FCSTD DOCUMENT  (FreeCAD 0.17R13541 (Git))
Label: qd_device_parts_v2
License: All rights reserved
LicenseURL: http://en.wikipedia.org/wiki/All_rights_reserved
objects: Sketcher::SketchObject×30, Part::Feature×24, App::DocumentObjectGroup×1
note: 54 computed .brp shape members not serialized (recipe doc carries the construction recipe); baked Part::Feature solids carry a one-line shape summary decoded from their .brp

FEATURE [App::DocumentObjectGroup] qqd_v2_6  label="qqd-v2-6"
FEATURE [Part::Feature] Shape
  shape: bbox 3400 x 150 x 2e-07 mm, 0 faces, 0 solids (baked)
FEATURE [Part::Feature] Shape001
  shape: bbox 1400 x 856.2 x 2e-07 mm, 0 faces, 0 solids (baked)
FEATURE [Part::Feature] Shape002
  shape: bbox 842.8 x 945 x 2e-07 mm, 0 faces, 0 solids (baked)
FEATURE [Part::Feature] Shape003
  shape: bbox 1400 x 856.2 x 2e-07 mm, 0 faces, 0 solids (baked)
FEATURE [Part::Feature] Shape004
  shape: bbox 1400 x 856.2 x 2e-07 mm, 0 faces, 0 solids (baked)
FEATURE [Part::Feature] Shape005
  shape: bbox 1400 x 856.2 x 2e-07 mm, 0 faces, 0 solids (baked)
FEATURE [Part::Feature] Shape006
  shape: bbox 2530 x 825 x 2e-07 mm, 0 faces, 0 solids (baked)
FEATURE [Part::Feature] Shape007
  shape: bbox 1180 x 825 x 2e-07 mm, 0 faces, 0 solids (baked)
FEATURE [Part::Feature] Shape008
  shape: bbox 1180 x 825 x 2e-07 mm, 0 faces, 0 solids (baked)
FEATURE [Part::Feature] Shape009
  shape: bbox 225 x 945 x 2e-07 mm, 0 faces, 0 solids (baked)
FEATURE [Part::Feature] Shape010
  shape: bbox 495 x 945 x 2e-07 mm, 0 faces, 0 solids (baked)
FEATURE [Part::Feature] Shape011
  shape: bbox 360 x 945 x 2e-07 mm, 0 faces, 0 solids (baked)
FEATURE [Part::Feature] Shape012
  shape: bbox 630 x 945 x 2e-07 mm, 0 faces, 0 solids (baked)
FEATURE [Part::Feature] Shape013
  shape: bbox 150 x 945 x 2e-07 mm, 0 faces, 0 solids (baked)
FEATURE [Part::Feature] Shape014
  shape: bbox 360 x 945 x 2e-07 mm, 0 faces, 0 solids (baked)
FEATURE [Part::Feature] Shape015
  shape: bbox 630 x 945 x 2e-07 mm, 0 faces, 0 solids (baked)
FEATURE [Part::Feature] Shape016
  shape: bbox 225 x 945 x 2e-07 mm, 0 faces, 0 solids (baked)
FEATURE [Part::Feature] Shape017
  shape: bbox 495 x 945 x 2e-07 mm, 0 faces, 0 solids (baked)
FEATURE [Part::Feature] Shape018
  shape: bbox 584 x 945 x 2e-07 mm, 0 faces, 0 solids (baked)
FEATURE [Part::Feature] Shape019
  shape: bbox 780 x 945 x 2e-07 mm, 0 faces, 0 solids (baked)
FEATURE [Part::Feature] Shape020
  shape: bbox 679 x 945 x 2e-07 mm, 0 faces, 0 solids (baked)
FEATURE [Part::Feature] Shape021
  shape: bbox 679 x 945 x 2e-07 mm, 0 faces, 0 solids (baked)
FEATURE [Part::Feature] Shape022
  shape: bbox 780 x 945 x 2e-07 mm, 0 faces, 0 solids (baked)
FEATURE [Part::Feature] Shape023
  shape: bbox 584 x 945 x 2e-07 mm, 0 faces, 0 solids (baked)
FEATURE [Sketcher::SketchObject] Sketch
  sketch-geometry (4):
    g0: LineSegment StartX=1699.91 StartY=105 StartZ=0 EndX=-1699.91 EndY=105 EndZ=0
    g1: LineSegment StartX=-1699.91 StartY=105 StartZ=0 EndX=-1699.91 EndY=-45 EndZ=0
    g2: LineSegment StartX=-1699.91 StartY=-45 StartZ=0 EndX=1699.91 EndY=-45 EndZ=0
    g3: LineSegment StartX=1699.91 StartY=-45 StartZ=0 EndX=1699.91 EndY=105 EndZ=0
  constraints (8):
    c: Horizontal(g0)
    c: Coincident(g0,g1)
    c: Vertical(g1)
    c: Coincident(g1,g2)
    c: Horizontal(g2)
    c: Coincident(g2,g3)
    c: Vertical(g3)
    c: Coincident(g3,g0)
FEATURE [Sketcher::SketchObject] Sketch001
  sketch-geometry (7):
    g0: LineSegment StartX=450 StartY=-970 StartZ=0 EndX=170 EndY=-185 EndZ=0
    g1: LineSegment StartX=170 StartY=-185 StartZ=0 EndX=170 EndY=-25 EndZ=0
    g2: LineSegment StartX=170 StartY=-25 StartZ=0 EndX=90 EndY=-25 EndZ=0
    g3: LineSegment StartX=90 StartY=-25 StartZ=0 EndX=90 EndY=-145 EndZ=0
    g4: LineSegment StartX=90 StartY=-145 StartZ=0 EndX=133.61 EndY=-355.94 EndZ=0
    g5: LineSegment StartX=133.61 StartY=-355.94 StartZ=0 EndX=300 EndY=-970 EndZ=0
    g6: LineSegment StartX=300 StartY=-970 StartZ=0 EndX=450 EndY=-970 EndZ=0
  constraints (11):
    c: Coincident(g0,g1)
    c: Vertical(g1)
    c: Coincident(g1,g2)
    c: Horizontal(g2)
    c: Coincident(g2,g3)
    c: Vertical(g3)
    c: Coincident(g3,g4)
    c: Coincident(g4,g5)
    c: Coincident(g5,g6)
    c: Horizontal(g6)
    c: Coincident(g6,g0)
FEATURE [Sketcher::SketchObject] Sketch002
  sketch-geometry (6):
    g0: LineSegment StartX=-40 StartY=-205 StartZ=0 EndX=-40 EndY=-25 EndZ=0
    g1: LineSegment StartX=-40 StartY=-25 StartZ=0 EndX=40 EndY=-25 EndZ=0
    g2: LineSegment StartX=40 StartY=-25 StartZ=0 EndX=40 EndY=-205 EndZ=0
    g3: LineSegment StartX=40 StartY=-205 StartZ=0 EndX=75 EndY=-970 EndZ=0
    g4: LineSegment StartX=75 StartY=-970 StartZ=0 EndX=-75 EndY=-970 EndZ=0
    g5: LineSegment StartX=-75 StartY=-970 StartZ=0 EndX=-40 EndY=-205 EndZ=0
  constraints (10):
    c: Vertical(g0)
    c: Coincident(g0,g1)
    c: Horizontal(g1)
    c: Coincident(g1,g2)
    c: Vertical(g2)
    c: Coincident(g2,g3)
    c: Coincident(g3,g4)
    c: Horizontal(g4)
    c: Coincident(g4,g5)
    c: Coincident(g5,g0)
FEATURE [Sketcher::SketchObject] Sketch003
  sketch-geometry (8):
    g0: LineSegment StartX=-369.81 StartY=-145 StartZ=0 EndX=369.81 EndY=-145 EndZ=0
    g1: LineSegment StartX=369.81 StartY=-145 StartZ=0 EndX=1265 EndY=-970 EndZ=0
    g2: LineSegment StartX=1265 StartY=-970 StartZ=0 EndX=905 EndY=-970 EndZ=0
    g3: LineSegment StartX=905 StartY=-970 StartZ=0 EndX=448.323 EndY=-535 EndZ=0
    g4: LineSegment StartX=448.323 StartY=-535 StartZ=0 EndX=-448.323 EndY=-535 EndZ=0
    g5: LineSegment StartX=-448.323 StartY=-535 StartZ=0 EndX=-905 EndY=-970 EndZ=0
    g6: LineSegment StartX=-905 StartY=-970 StartZ=0 EndX=-1265 EndY=-970 EndZ=0
    g7: LineSegment StartX=-1265 StartY=-970 StartZ=0 EndX=-369.81 EndY=-145 EndZ=0
  constraints (12):
    c: Horizontal(g0)
    c: Coincident(g0,g1)
    c: Coincident(g1,g2)
    c: Horizontal(g2)
    c: Coincident(g2,g3)
    c: Coincident(g3,g4)
    c: Horizontal(g4)
    c: Coincident(g4,g5)
    c: Coincident(g5,g6)
    c: Horizontal(g6)
    c: Coincident(g6,g7)
    c: Coincident(g7,g0)
FEATURE [Sketcher::SketchObject] Sketch004
  sketch-geometry (7):
    g0: LineSegment StartX=-450 StartY=-970 StartZ=0 EndX=-170 EndY=-185 EndZ=0
    g1: LineSegment StartX=-170 StartY=-185 StartZ=0 EndX=-170 EndY=-25 EndZ=0
    g2: LineSegment StartX=-170 StartY=-25 StartZ=0 EndX=-90 EndY=-25 EndZ=0
    g3: LineSegment StartX=-90 StartY=-25 StartZ=0 EndX=-90 EndY=-145 EndZ=0
    g4: LineSegment StartX=-90 StartY=-145 StartZ=0 EndX=-133.61 EndY=-355.94 EndZ=0
    g5: LineSegment StartX=-133.61 StartY=-355.94 StartZ=0 EndX=-300 EndY=-970 EndZ=0
    g6: LineSegment StartX=-300 StartY=-970 StartZ=0 EndX=-450 EndY=-970 EndZ=0
  constraints (11):
    c: Coincident(g0,g1)
    c: Vertical(g1)
    c: Coincident(g1,g2)
    c: Horizontal(g2)
    c: Coincident(g2,g3)
    c: Vertical(g3)
    c: Coincident(g3,g4)
    c: Coincident(g4,g5)
    c: Coincident(g5,g6)
    c: Horizontal(g6)
    c: Coincident(g6,g0)
FEATURE [Sketcher::SketchObject] Sketch005
  sketch-geometry (7):
    g0: LineSegment StartX=-105 StartY=-25 StartZ=0 EndX=-25 EndY=-25 EndZ=0
    g1: LineSegment StartX=-25 StartY=-25 StartZ=0 EndX=-25 EndY=-145 EndZ=0
    g2: LineSegment StartX=-25 StartY=-145 StartZ=0 EndX=-53.655 EndY=-503.461 EndZ=0
    g3: LineSegment StartX=-53.655 StartY=-503.461 StartZ=0 EndX=-100 EndY=-970 EndZ=0
    g4: LineSegment StartX=-100 StartY=-970 StartZ=0 EndX=-250 EndY=-970 EndZ=0
    g5: LineSegment StartX=-250 StartY=-970 StartZ=0 EndX=-105 EndY=-205 EndZ=0
    g6: LineSegment StartX=-105 StartY=-205 StartZ=0 EndX=-105 EndY=-25 EndZ=0
  constraints (11):
    c: Horizontal(g0)
    c: Coincident(g0,g1)
    c: Vertical(g1)
    c: Coincident(g1,g2)
    c: Coincident(g2,g3)
    c: Coincident(g3,g4)
    c: Horizontal(g4)
    c: Coincident(g4,g5)
    c: Coincident(g5,g6)
    c: Vertical(g6)
    c: Coincident(g6,g0)
FEATURE [Sketcher::SketchObject] Sketch006
  sketch-geometry (7):
    g0: LineSegment StartX=-251.765 StartY=595 StartZ=0 EndX=-448.323 EndY=595 EndZ=0
    g1: LineSegment StartX=-448.323 StartY=595 StartZ=0 EndX=-905 EndY=1030 EndZ=0
    g2: LineSegment StartX=-905 StartY=1030 StartZ=0 EndX=-1265 EndY=1030 EndZ=0
    g3: LineSegment StartX=-1265 StartY=1030 StartZ=0 EndX=-369.81 EndY=205 EndZ=0
    g4: LineSegment StartX=-369.81 StartY=205 StartZ=0 EndX=-85 EndY=205 EndZ=0
    g5: LineSegment StartX=-85 StartY=205 StartZ=0 EndX=-85 EndY=265 EndZ=0
    g6: LineSegment StartX=-85 StartY=265 StartZ=0 EndX=-251.765 EndY=595 EndZ=0
  constraints (11):
    c: Horizontal(g0)
    c: Coincident(g0,g1)
    c: Coincident(g1,g2)
    c: Horizontal(g2)
    c: Coincident(g2,g3)
    c: Coincident(g3,g4)
    c: Horizontal(g4)
    c: Coincident(g4,g5)
    c: Vertical(g5)
    c: Coincident(g5,g6)
    c: Coincident(g6,g0)
FEATURE [Sketcher::SketchObject] Sketch007
  sketch-geometry (8):
    g0: LineSegment StartX=-1685.36 StartY=-431.669 StartZ=0 EndX=-1198.72 EndY=-881.17 EndZ=0
    g1: LineSegment StartX=-1198.72 StartY=-881.17 StartZ=0 EndX=-720.86 EndY=-499.639 EndZ=0
    g2: LineSegment StartX=-720.86 StartY=-499.639 StartZ=0 EndX=-362.004 EndY=-165 EndZ=0
    g3: LineSegment StartX=-362.004 StartY=-165 StartZ=0 EndX=-305 EndY=-165 EndZ=0
    g4: LineSegment StartX=-305 StartY=-165 StartZ=0 EndX=-285 EndY=-145 EndZ=0
    g5: LineSegment StartX=-285 StartY=-145 StartZ=0 EndX=-285 EndY=-25 EndZ=0
    g6: LineSegment StartX=-285 StartY=-25 StartZ=0 EndX=-859.697 EndY=-25 EndZ=0
    g7: LineSegment StartX=-859.697 StartY=-25 StartZ=0 EndX=-1685.36 EndY=-431.669 EndZ=0
  constraints (11):
    c: Coincident(g0,g1)
    c: Coincident(g1,g2)
    c: Coincident(g2,g3)
    c: Horizontal(g3)
    c: Coincident(g3,g4)
    c: Coincident(g4,g5)
    c: Vertical(g5)
    c: Coincident(g5,g6)
    c: Horizontal(g6)
    c: Coincident(g6,g7)
    c: Coincident(g7,g0)
FEATURE [Sketcher::SketchObject] Sketch008
  sketch-geometry (8):
    g0: LineSegment StartX=1685.36 StartY=-431.669 StartZ=0 EndX=1198.72 EndY=-881.17 EndZ=0
    g1: LineSegment StartX=1198.72 StartY=-881.17 StartZ=0 EndX=720.86 EndY=-499.639 EndZ=0
    g2: LineSegment StartX=720.86 StartY=-499.639 StartZ=0 EndX=362.004 EndY=-165 EndZ=0
    g3: LineSegment StartX=362.004 StartY=-165 StartZ=0 EndX=305 EndY=-165 EndZ=0
    g4: LineSegment StartX=305 StartY=-165 StartZ=0 EndX=285 EndY=-145 EndZ=0
    g5: LineSegment StartX=285 StartY=-145 StartZ=0 EndX=285 EndY=-25 EndZ=0
    g6: LineSegment StartX=285 StartY=-25 StartZ=0 EndX=859.697 EndY=-25 EndZ=0
    g7: LineSegment StartX=859.697 StartY=-25 StartZ=0 EndX=1685.36 EndY=-431.669 EndZ=0
  constraints (11):
    c: Coincident(g0,g1)
    c: Coincident(g1,g2)
    c: Coincident(g2,g3)
    c: Horizontal(g3)
    c: Coincident(g3,g4)
    c: Coincident(g4,g5)
    c: Vertical(g5)
    c: Coincident(g5,g6)
    c: Horizontal(g6)
    c: Coincident(g6,g7)
    c: Coincident(g7,g0)
FEATURE [Sketcher::SketchObject] Sketch009
  sketch-geometry (8):
    g0: LineSegment StartX=-1685.36 StartY=491.669 StartZ=0 EndX=-1198.72 EndY=941.17 EndZ=0
    g1: LineSegment StartX=-1198.72 StartY=941.17 StartZ=0 EndX=-720.86 EndY=559.639 EndZ=0
    g2: LineSegment StartX=-720.86 StartY=559.639 StartZ=0 EndX=-362.004 EndY=225 EndZ=0
    g3: LineSegment StartX=-362.004 StartY=225 StartZ=0 EndX=-305 EndY=225 EndZ=0
    g4: LineSegment StartX=-305 StartY=225 StartZ=0 EndX=-285 EndY=205 EndZ=0
    g5: LineSegment StartX=-285 StartY=205 StartZ=0 EndX=-285 EndY=85 EndZ=0
    g6: LineSegment StartX=-285 StartY=85 StartZ=0 EndX=-859.697 EndY=85 EndZ=0
    g7: LineSegment StartX=-859.697 StartY=85 StartZ=0 EndX=-1685.36 EndY=491.669 EndZ=0
  constraints (11):
    c: Coincident(g0,g1)
    c: Coincident(g1,g2)
    c: Coincident(g2,g3)
    c: Horizontal(g3)
    c: Coincident(g3,g4)
    c: Coincident(g4,g5)
    c: Vertical(g5)
    c: Coincident(g5,g6)
    c: Horizontal(g6)
    c: Coincident(g6,g7)
    c: Coincident(g7,g0)
FEATURE [Sketcher::SketchObject] Sketch010
  sketch-geometry (8):
    g0: LineSegment StartX=402.551 StartY=853.805 StartZ=0 EndX=105 EndY=265 EndZ=0
    g1: LineSegment StartX=105 StartY=265 StartZ=0 EndX=105 EndY=85 EndZ=0
    g2: LineSegment StartX=105 StartY=85 StartZ=0 EndX=-105 EndY=85 EndZ=0
    g3: LineSegment StartX=-105 StartY=85 StartZ=0 EndX=-105 EndY=265 EndZ=0
    g4: LineSegment StartX=-105 StartY=265 StartZ=0 EndX=-402.551 EndY=853.805 EndZ=0
    g5: LineSegment StartX=-402.551 StartY=853.805 StartZ=0 EndX=-421.41 EndY=1030 EndZ=0
    g6: LineSegment StartX=-421.41 StartY=1030 StartZ=0 EndX=421.41 EndY=1030 EndZ=0
    g7: LineSegment StartX=421.41 StartY=1030 StartZ=0 EndX=402.551 EndY=853.805 EndZ=0
  constraints (12):
    c: Coincident(g0,g1)
    c: Vertical(g1)
    c: Coincident(g1,g2)
    c: Horizontal(g2)
    c: Coincident(g2,g3)
    c: Vertical(g3)
    c: Coincident(g3,g4)
    c: Coincident(g4,g5)
    c: Coincident(g5,g6)
    c: Horizontal(g6)
    c: Coincident(g6,g7)
    c: Coincident(g7,g0)
FEATURE [Sketcher::SketchObject] Sketch011
  sketch-geometry (7):
    g0: LineSegment StartX=251.765 StartY=595 StartZ=0 EndX=448.323 EndY=595 EndZ=0
    g1: LineSegment StartX=448.323 StartY=595 StartZ=0 EndX=905 EndY=1030 EndZ=0
    g2: LineSegment StartX=905 StartY=1030 StartZ=0 EndX=1265 EndY=1030 EndZ=0
    g3: LineSegment StartX=1265 StartY=1030 StartZ=0 EndX=369.81 EndY=205 EndZ=0
    g4: LineSegment StartX=369.81 StartY=205 StartZ=0 EndX=85 EndY=205 EndZ=0
    g5: LineSegment StartX=85 StartY=205 StartZ=0 EndX=85 EndY=265 EndZ=0
    g6: LineSegment StartX=85 StartY=265 StartZ=0 EndX=251.765 EndY=595 EndZ=0
  constraints (11):
    c: Horizontal(g0)
    c: Coincident(g0,g1)
    c: Coincident(g1,g2)
    c: Horizontal(g2)
    c: Coincident(g2,g3)
    c: Coincident(g3,g4)
    c: Horizontal(g4)
    c: Coincident(g4,g5)
    c: Vertical(g5)
    c: Coincident(g5,g6)
    c: Coincident(g6,g0)
FEATURE [Sketcher::SketchObject] Sketch012
  sketch-geometry (8):
    g0: LineSegment StartX=1685.36 StartY=491.669 StartZ=0 EndX=1198.72 EndY=941.17 EndZ=0
    g1: LineSegment StartX=1198.72 StartY=941.17 StartZ=0 EndX=720.86 EndY=559.639 EndZ=0
    g2: LineSegment StartX=720.86 StartY=559.639 StartZ=0 EndX=362.004 EndY=225 EndZ=0
    g3: LineSegment StartX=362.004 StartY=225 StartZ=0 EndX=305 EndY=225 EndZ=0
    g4: LineSegment StartX=305 StartY=225 StartZ=0 EndX=285 EndY=205 EndZ=0
    g5: LineSegment StartX=285 StartY=205 StartZ=0 EndX=285 EndY=85 EndZ=0
    g6: LineSegment StartX=285 StartY=85 StartZ=0 EndX=859.697 EndY=85 EndZ=0
    g7: LineSegment StartX=859.697 StartY=85 StartZ=0 EndX=1685.36 EndY=491.669 EndZ=0
  constraints (11):
    c: Coincident(g0,g1)
    c: Coincident(g1,g2)
    c: Coincident(g2,g3)
    c: Horizontal(g3)
    c: Coincident(g3,g4)
    c: Coincident(g4,g5)
    c: Vertical(g5)
    c: Coincident(g5,g6)
    c: Horizontal(g6)
    c: Coincident(g6,g7)
    c: Coincident(g7,g0)
FEATURE [Sketcher::SketchObject] Sketch013
  sketch-geometry (8):
    g0: LineSegment StartX=-155 StartY=-25 StartZ=0 EndX=-155 EndY=-145 EndZ=0
    g1: LineSegment StartX=-155 StartY=-145 StartZ=0 EndX=-170 EndY=-185 EndZ=0
    g2: LineSegment StartX=-170 StartY=-185 StartZ=0 EndX=-269.574 EndY=-464.164 EndZ=0
    g3: LineSegment StartX=-269.574 StartY=-464.164 StartZ=0 EndX=-470 EndY=-970 EndZ=0
    g4: LineSegment StartX=-470 StartY=-970 StartZ=0 EndX=-650 EndY=-970 EndZ=0
    g5: LineSegment StartX=-650 StartY=-970 StartZ=0 EndX=-235 EndY=-165 EndZ=0
    g6: LineSegment StartX=-235 StartY=-165 StartZ=0 EndX=-235 EndY=-25 EndZ=0
    g7: LineSegment StartX=-235 StartY=-25 StartZ=0 EndX=-155 EndY=-25 EndZ=0
  constraints (12):
    c: Vertical(g0)
    c: Coincident(g0,g1)
    c: Coincident(g1,g2)
    c: Coincident(g2,g3)
    c: Coincident(g3,g4)
    c: Horizontal(g4)
    c: Coincident(g4,g5)
    c: Coincident(g5,g6)
    c: Vertical(g6)
    c: Coincident(g6,g7)
    c: Horizontal(g7)
    c: Coincident(g7,g0)
FEATURE [Sketcher::SketchObject] Sketch014
  sketch-geometry (7):
    g0: LineSegment StartX=-850 StartY=-970 StartZ=0 EndX=-300 EndY=-145 EndZ=0
    g1: LineSegment StartX=-300 StartY=-145 StartZ=0 EndX=-300 EndY=-25 EndZ=0
    g2: LineSegment StartX=-300 StartY=-25 StartZ=0 EndX=-220 EndY=-25 EndZ=0
    g3: LineSegment StartX=-220 StartY=-25 StartZ=0 EndX=-220 EndY=-145 EndZ=0
    g4: LineSegment StartX=-220 StartY=-145 StartZ=0 EndX=-368.439 EndY=-423.84 EndZ=0
    g5: LineSegment StartX=-368.439 StartY=-423.84 StartZ=0 EndX=-670 EndY=-970 EndZ=0
    g6: LineSegment StartX=-670 StartY=-970 StartZ=0 EndX=-850 EndY=-970 EndZ=0
  constraints (11):
    c: Coincident(g0,g1)
    c: Vertical(g1)
    c: Coincident(g1,g2)
    c: Horizontal(g2)
    c: Coincident(g2,g3)
    c: Vertical(g3)
    c: Coincident(g3,g4)
    c: Coincident(g4,g5)
    c: Coincident(g5,g6)
    c: Horizontal(g6)
    c: Coincident(g6,g0)
FEATURE [Sketcher::SketchObject] Sketch015
  sketch-geometry (8):
    g0: LineSegment StartX=155 StartY=-25 StartZ=0 EndX=155 EndY=-145 EndZ=0
    g1: LineSegment StartX=155 StartY=-145 StartZ=0 EndX=170 EndY=-185 EndZ=0
    g2: LineSegment StartX=170 StartY=-185 StartZ=0 EndX=269.574 EndY=-464.164 EndZ=0
    g3: LineSegment StartX=269.574 StartY=-464.164 StartZ=0 EndX=470 EndY=-970 EndZ=0
    g4: LineSegment StartX=470 StartY=-970 StartZ=0 EndX=650 EndY=-970 EndZ=0
    g5: LineSegment StartX=650 StartY=-970 StartZ=0 EndX=235 EndY=-165 EndZ=0
    g6: LineSegment StartX=235 StartY=-165 StartZ=0 EndX=235 EndY=-25 EndZ=0
    g7: LineSegment StartX=235 StartY=-25 StartZ=0 EndX=155 EndY=-25 EndZ=0
  constraints (12):
    c: Vertical(g0)
    c: Coincident(g0,g1)
    c: Coincident(g1,g2)
    c: Coincident(g2,g3)
    c: Coincident(g3,g4)
    c: Horizontal(g4)
    c: Coincident(g4,g5)
    c: Coincident(g5,g6)
    c: Vertical(g6)
    c: Coincident(g6,g7)
    c: Horizontal(g7)
    c: Coincident(g7,g0)
FEATURE [Sketcher::SketchObject] Sketch016
  sketch-geometry (6):
    g0: LineSegment StartX=-674.039 StartY=1030 StartZ=0 EndX=-170 EndY=245 EndZ=0
    g1: LineSegment StartX=-170 StartY=245 StartZ=0 EndX=-170 EndY=85 EndZ=0
    g2: LineSegment StartX=-170 StartY=85 StartZ=0 EndX=-90 EndY=85 EndZ=0
    g3: LineSegment StartX=-90 StartY=85 StartZ=0 EndX=-90 EndY=245 EndZ=0
    g4: LineSegment StartX=-90 StartY=245 StartZ=0 EndX=-524.039 EndY=1030 EndZ=0
    g5: LineSegment StartX=-524.039 StartY=1030 StartZ=0 EndX=-674.039 EndY=1030 EndZ=0
  constraints (10):
    c: Coincident(g0,g1)
    c: Vertical(g1)
    c: Coincident(g1,g2)
    c: Horizontal(g2)
    c: Coincident(g2,g3)
    c: Vertical(g3)
    c: Coincident(g3,g4)
    c: Coincident(g4,g5)
    c: Horizontal(g5)
    c: Coincident(g5,g0)
FEATURE [Sketcher::SketchObject] Sketch017
  sketch-geometry (6):
    g0: LineSegment StartX=1000 StartY=1030 StartZ=0 EndX=300 EndY=205 EndZ=0
    g1: LineSegment StartX=300 StartY=205 StartZ=0 EndX=300 EndY=85 EndZ=0
    g2: LineSegment StartX=300 StartY=85 StartZ=0 EndX=220 EndY=85 EndZ=0
    g3: LineSegment StartX=220 StartY=85 StartZ=0 EndX=220 EndY=205 EndZ=0
    g4: LineSegment StartX=220 StartY=205 StartZ=0 EndX=850 EndY=1030 EndZ=0
    g5: LineSegment StartX=850 StartY=1030 StartZ=0 EndX=1000 EndY=1030 EndZ=0
  constraints (10):
    c: Coincident(g0,g1)
    c: Vertical(g1)
    c: Coincident(g1,g2)
    c: Horizontal(g2)
    c: Coincident(g2,g3)
    c: Vertical(g3)
    c: Coincident(g3,g4)
    c: Coincident(g4,g5)
    c: Horizontal(g5)
    c: Coincident(g5,g0)
FEATURE [Sketcher::SketchObject] Sketch018
  sketch-geometry (7):
    g0: LineSegment StartX=850 StartY=-970 StartZ=0 EndX=300 EndY=-145 EndZ=0
    g1: LineSegment StartX=300 StartY=-145 StartZ=0 EndX=300 EndY=-25 EndZ=0
    g2: LineSegment StartX=300 StartY=-25 StartZ=0 EndX=220 EndY=-25 EndZ=0
    g3: LineSegment StartX=220 StartY=-25 StartZ=0 EndX=220 EndY=-145 EndZ=0
    g4: LineSegment StartX=220 StartY=-145 StartZ=0 EndX=368.439 EndY=-423.84 EndZ=0
    g5: LineSegment StartX=368.439 StartY=-423.84 StartZ=0 EndX=670 EndY=-970 EndZ=0
    g6: LineSegment StartX=670 StartY=-970 StartZ=0 EndX=850 EndY=-970 EndZ=0
  constraints (11):
    c: Coincident(g0,g1)
    c: Vertical(g1)
    c: Coincident(g1,g2)
    c: Horizontal(g2)
    c: Coincident(g2,g3)
    c: Vertical(g3)
    c: Coincident(g3,g4)
    c: Coincident(g4,g5)
    c: Coincident(g5,g6)
    c: Horizontal(g6)
    c: Coincident(g6,g0)
FEATURE [Sketcher::SketchObject] Sketch019
  sketch-geometry (6):
    g0: LineSegment StartX=-1000 StartY=1030 StartZ=0 EndX=-300 EndY=205 EndZ=0
    g1: LineSegment StartX=-300 StartY=205 StartZ=0 EndX=-300 EndY=85 EndZ=0
    g2: LineSegment StartX=-300 StartY=85 StartZ=0 EndX=-220 EndY=85 EndZ=0
    g3: LineSegment StartX=-220 StartY=85 StartZ=0 EndX=-220 EndY=205 EndZ=0
    g4: LineSegment StartX=-220 StartY=205 StartZ=0 EndX=-850 EndY=1030 EndZ=0
    g5: LineSegment StartX=-850 StartY=1030 StartZ=0 EndX=-1000 EndY=1030 EndZ=0
  constraints (10):
    c: Coincident(g0,g1)
    c: Vertical(g1)
    c: Coincident(g1,g2)
    c: Horizontal(g2)
    c: Coincident(g2,g3)
    c: Vertical(g3)
    c: Coincident(g3,g4)
    c: Coincident(g4,g5)
    c: Horizontal(g5)
    c: Coincident(g5,g0)
FEATURE [Sketcher::SketchObject] Sketch020
  sketch-geometry (6):
    g0: LineSegment StartX=-235 StartY=85 StartZ=0 EndX=-155 EndY=85 EndZ=0
    g1: LineSegment StartX=-155 StartY=85 StartZ=0 EndX=-155 EndY=205 EndZ=0
    g2: LineSegment StartX=-155 StartY=205 StartZ=0 EndX=-684.039 EndY=1030 EndZ=0
    g3: LineSegment StartX=-684.039 StartY=1030 StartZ=0 EndX=-834.039 EndY=1030 EndZ=0
    g4: LineSegment StartX=-834.039 StartY=1030 StartZ=0 EndX=-235 EndY=225 EndZ=0
    g5: LineSegment StartX=-235 StartY=225 StartZ=0 EndX=-235 EndY=85 EndZ=0
  constraints (10):
    c: Horizontal(g0)
    c: Coincident(g0,g1)
    c: Vertical(g1)
    c: Coincident(g1,g2)
    c: Coincident(g2,g3)
    c: Horizontal(g3)
    c: Coincident(g3,g4)
    c: Coincident(g4,g5)
    c: Vertical(g5)
    c: Coincident(g5,g0)
FEATURE [Sketcher::SketchObject] Sketch021
  sketch-geometry (6):
    g0: LineSegment StartX=235 StartY=85 StartZ=0 EndX=155 EndY=85 EndZ=0
    g1: LineSegment StartX=155 StartY=85 StartZ=0 EndX=155 EndY=205 EndZ=0
    g2: LineSegment StartX=155 StartY=205 StartZ=0 EndX=684.039 EndY=1030 EndZ=0
    g3: LineSegment StartX=684.039 StartY=1030 StartZ=0 EndX=834.039 EndY=1030 EndZ=0
    g4: LineSegment StartX=834.039 StartY=1030 StartZ=0 EndX=235 EndY=225 EndZ=0
    g5: LineSegment StartX=235 StartY=225 StartZ=0 EndX=235 EndY=85 EndZ=0
  constraints (10):
    c: Horizontal(g0)
    c: Coincident(g0,g1)
    c: Vertical(g1)
    c: Coincident(g1,g2)
    c: Coincident(g2,g3)
    c: Horizontal(g3)
    c: Coincident(g3,g4)
    c: Coincident(g4,g5)
    c: Vertical(g5)
    c: Coincident(g5,g0)
FEATURE [Sketcher::SketchObject] Sketch022
  sketch-geometry (6):
    g0: LineSegment StartX=674.039 StartY=1030 StartZ=0 EndX=170 EndY=245 EndZ=0
    g1: LineSegment StartX=170 StartY=245 StartZ=0 EndX=170 EndY=85 EndZ=0
    g2: LineSegment StartX=170 StartY=85 StartZ=0 EndX=90 EndY=85 EndZ=0
    g3: LineSegment StartX=90 StartY=85 StartZ=0 EndX=90 EndY=245 EndZ=0
    g4: LineSegment StartX=90 StartY=245 StartZ=0 EndX=524.039 EndY=1030 EndZ=0
    g5: LineSegment StartX=524.039 StartY=1030 StartZ=0 EndX=674.039 EndY=1030 EndZ=0
  constraints (10):
    c: Coincident(g0,g1)
    c: Vertical(g1)
    c: Coincident(g1,g2)
    c: Horizontal(g2)
    c: Coincident(g2,g3)
    c: Vertical(g3)
    c: Coincident(g3,g4)
    c: Coincident(g4,g5)
    c: Horizontal(g5)
    c: Coincident(g5,g0)
FEATURE [Sketcher::SketchObject] Sketch023
  sketch-geometry (7):
    g0: LineSegment StartX=105 StartY=-25 StartZ=0 EndX=25 EndY=-25 EndZ=0
    g1: LineSegment StartX=25 StartY=-25 StartZ=0 EndX=25 EndY=-145 EndZ=0
    g2: LineSegment StartX=25 StartY=-145 StartZ=0 EndX=53.655 EndY=-503.461 EndZ=0
    g3: LineSegment StartX=53.655 StartY=-503.461 StartZ=0 EndX=100 EndY=-970 EndZ=0
    g4: LineSegment StartX=100 StartY=-970 StartZ=0 EndX=250 EndY=-970 EndZ=0
    g5: LineSegment StartX=250 StartY=-970 StartZ=0 EndX=105 EndY=-205 EndZ=0
    g6: LineSegment StartX=105 StartY=-205 StartZ=0 EndX=105 EndY=-25 EndZ=0
  constraints (11):
    c: Horizontal(g0)
    c: Coincident(g0,g1)
    c: Vertical(g1)
    c: Coincident(g1,g2)
    c: Coincident(g2,g3)
    c: Coincident(g3,g4)
    c: Horizontal(g4)
    c: Coincident(g4,g5)
    c: Coincident(g5,g6)
    c: Vertical(g6)
    c: Coincident(g6,g0)
FEATURE [Sketcher::SketchObject] Sketch024
  sketch-geometry (26):
    g0: LineSegment StartX=-369.81 StartY=-145 StartZ=0 EndX=369.81 EndY=-145 EndZ=0
    g1: LineSegment StartX=369.81 StartY=-145 StartZ=0 EndX=1265 EndY=-970 EndZ=0
    g2: LineSegment StartX=1265 StartY=-970 StartZ=0 EndX=905 EndY=-970 EndZ=0
    g3: LineSegment StartX=905 StartY=-970 StartZ=0 EndX=448.323 EndY=-535 EndZ=0
    g4: LineSegment StartX=448.323 StartY=-535 StartZ=0 EndX=-448.323 EndY=-535 EndZ=0
    g5: LineSegment StartX=-448.323 StartY=-535 StartZ=0 EndX=-905 EndY=-970 EndZ=0
    g6: LineSegment StartX=-905 StartY=-970 StartZ=0 EndX=-1265 EndY=-970 EndZ=0
    g7: LineSegment StartX=-1265 StartY=-970 StartZ=0 EndX=-369.81 EndY=-145 EndZ=0
    g8: LineSegment StartX=-251.765 StartY=595 StartZ=0 EndX=-448.323 EndY=595 EndZ=0
    g9: LineSegment StartX=-448.323 StartY=595 StartZ=0 EndX=-905 EndY=1030 EndZ=0
    g10: LineSegment StartX=-905 StartY=1030 StartZ=0 EndX=-1265 EndY=1030 EndZ=0
    g11: LineSegment StartX=-1265 StartY=1030 StartZ=0 EndX=-369.81 EndY=205 EndZ=0
    g12: LineSegment StartX=-369.81 StartY=205 StartZ=0 EndX=-85 EndY=205 EndZ=0
    g13: LineSegment StartX=-85 StartY=205 StartZ=0 EndX=-85 EndY=265 EndZ=0
    g14: LineSegment StartX=-85 StartY=265 StartZ=0 EndX=-251.765 EndY=595 EndZ=0
    g15: LineSegment StartX=251.765 StartY=595 StartZ=0 EndX=448.323 EndY=595 EndZ=0
    g16: LineSegment StartX=448.323 StartY=595 StartZ=0 EndX=905 EndY=1030 EndZ=0
    g17: LineSegment StartX=905 StartY=1030 StartZ=0 EndX=1265 EndY=1030 EndZ=0
    g18: LineSegment StartX=1265 StartY=1030 StartZ=0 EndX=369.81 EndY=205 EndZ=0
    g19: LineSegment StartX=369.81 StartY=205 StartZ=0 EndX=85 EndY=205 EndZ=0
    g20: LineSegment StartX=85 StartY=205 StartZ=0 EndX=85 EndY=265 EndZ=0
    g21: LineSegment StartX=85 StartY=265 StartZ=0 EndX=251.765 EndY=595 EndZ=0
    g22: LineSegment StartX=1699.91 StartY=105 StartZ=0 EndX=-1699.91 EndY=105 EndZ=0
    g23: LineSegment StartX=-1699.91 StartY=105 StartZ=0 EndX=-1699.91 EndY=-45 EndZ=0
    g24: LineSegment StartX=-1699.91 StartY=-45 StartZ=0 EndX=1699.91 EndY=-45 EndZ=0
    g25: LineSegment StartX=1699.91 StartY=-45 StartZ=0 EndX=1699.91 EndY=105 EndZ=0
  constraints (42):
    c: Horizontal(g0)
    c: Coincident(g0,g1)
    c: Coincident(g1,g2)
    c: Horizontal(g2)
    c: Coincident(g2,g3)
    c: Coincident(g3,g4)
    c: Horizontal(g4)
    c: Coincident(g4,g5)
    c: Coincident(g5,g6)
    c: Horizontal(g6)
    c: Coincident(g6,g7)
    c: Coincident(g7,g0)
    c: Horizontal(g8)
    c: Coincident(g8,g9)
    c: Coincident(g9,g10)
    c: Horizontal(g10)
    c: Coincident(g10,g11)
    c: Coincident(g11,g12)
    c: Horizontal(g12)
    c: Coincident(g12,g13)
    c: Vertical(g13)
    c: Coincident(g13,g14)
    c: Coincident(g14,g8)
    c: Horizontal(g15)
    c: Coincident(g15,g16)
    c: Coincident(g16,g17)
    c: Horizontal(g17)
    c: Coincident(g17,g18)
    c: Coincident(g18,g19)
    c: Horizontal(g19)
    c: Coincident(g19,g20)
    c: Vertical(g20)
    c: Coincident(g20,g21)
    c: Coincident(g21,g15)
    c: Horizontal(g22)
    c: Coincident(g22,g23)
    c: Vertical(g23)
    c: Coincident(g23,g24)
    c: Horizontal(g24)
    c: Coincident(g24,g25)
    c: Vertical(g25)
    c: Coincident(g25,g22)
FEATURE [Sketcher::SketchObject] Sketch025
  sketch-geometry (82):
    g0: LineSegment StartX=-1685.36 StartY=-431.669 StartZ=0 EndX=-1198.72 EndY=-881.17 EndZ=0
    g1: LineSegment StartX=-1198.72 StartY=-881.17 StartZ=0 EndX=-720.86 EndY=-499.639 EndZ=0
    g2: LineSegment StartX=-720.86 StartY=-499.639 StartZ=0 EndX=-362.004 EndY=-165 EndZ=0
    g3: LineSegment StartX=-362.004 StartY=-165 StartZ=0 EndX=-305 EndY=-165 EndZ=0
    g4: LineSegment StartX=-305 StartY=-165 StartZ=0 EndX=-285 EndY=-145 EndZ=0
    g5: LineSegment StartX=-285 StartY=-145 StartZ=0 EndX=-285 EndY=-25 EndZ=0
    g6: LineSegment StartX=-285 StartY=-25 StartZ=0 EndX=-859.697 EndY=-25 EndZ=0
    g7: LineSegment StartX=-859.697 StartY=-25 StartZ=0 EndX=-1685.36 EndY=-431.669 EndZ=0
    g8: LineSegment StartX=1685.36 StartY=-431.669 StartZ=0 EndX=1198.72 EndY=-881.17 EndZ=0
    g9: LineSegment StartX=1198.72 StartY=-881.17 StartZ=0 EndX=720.86 EndY=-499.639 EndZ=0
    g10: LineSegment StartX=720.86 StartY=-499.639 StartZ=0 EndX=362.004 EndY=-165 EndZ=0
    g11: LineSegment StartX=362.004 StartY=-165 StartZ=0 EndX=305 EndY=-165 EndZ=0
    g12: LineSegment StartX=305 StartY=-165 StartZ=0 EndX=285 EndY=-145 EndZ=0
    g13: LineSegment StartX=285 StartY=-145 StartZ=0 EndX=285 EndY=-25 EndZ=0
    g14: LineSegment StartX=285 StartY=-25 StartZ=0 EndX=859.697 EndY=-25 EndZ=0
    g15: LineSegment StartX=859.697 StartY=-25 StartZ=0 EndX=1685.36 EndY=-431.669 EndZ=0
    g16: LineSegment StartX=-1685.36 StartY=491.669 StartZ=0 EndX=-1198.72 EndY=941.17 EndZ=0
    g17: LineSegment StartX=-1198.72 StartY=941.17 StartZ=0 EndX=-720.86 EndY=559.639 EndZ=0
    g18: LineSegment StartX=-720.86 StartY=559.639 StartZ=0 EndX=-362.004 EndY=225 EndZ=0
    g19: LineSegment StartX=-362.004 StartY=225 StartZ=0 EndX=-305 EndY=225 EndZ=0
    g20: LineSegment StartX=-305 StartY=225 StartZ=0 EndX=-285 EndY=205 EndZ=0
    g21: LineSegment StartX=-285 StartY=205 StartZ=0 EndX=-285 EndY=85 EndZ=0
    g22: LineSegment StartX=-285 StartY=85 StartZ=0 EndX=-859.697 EndY=85 EndZ=0
    g23: LineSegment StartX=-859.697 StartY=85 StartZ=0 EndX=-1685.36 EndY=491.669 EndZ=0
    g24: LineSegment StartX=402.551 StartY=853.805 StartZ=0 EndX=105 EndY=265 EndZ=0
    g25: LineSegment StartX=105 StartY=265 StartZ=0 EndX=105 EndY=85 EndZ=0
    g26: LineSegment StartX=105 StartY=85 StartZ=0 EndX=-105 EndY=85 EndZ=0
    g27: LineSegment StartX=-105 StartY=85 StartZ=0 EndX=-105 EndY=265 EndZ=0
    g28: LineSegment StartX=-105 StartY=265 StartZ=0 EndX=-402.551 EndY=853.805 EndZ=0
    g29: LineSegment StartX=-402.551 StartY=853.805 StartZ=0 EndX=-421.41 EndY=1030 EndZ=0
    g30: LineSegment StartX=-421.41 StartY=1030 StartZ=0 EndX=421.41 EndY=1030 EndZ=0
    g31: LineSegment StartX=421.41 StartY=1030 StartZ=0 EndX=402.551 EndY=853.805 EndZ=0
    g32: LineSegment StartX=1685.36 StartY=491.669 StartZ=0 EndX=1198.72 EndY=941.17 EndZ=0
    g33: LineSegment StartX=1198.72 StartY=941.17 StartZ=0 EndX=720.86 EndY=559.639 EndZ=0
    g34: LineSegment StartX=720.86 StartY=559.639 StartZ=0 EndX=362.004 EndY=225 EndZ=0
    g35: LineSegment StartX=362.004 StartY=225 StartZ=0 EndX=305 EndY=225 EndZ=0
    g36: LineSegment StartX=305 StartY=225 StartZ=0 EndX=285 EndY=205 EndZ=0
    g37: LineSegment StartX=285 StartY=205 StartZ=0 EndX=285 EndY=85 EndZ=0
    g38: LineSegment StartX=285 StartY=85 StartZ=0 EndX=859.697 EndY=85 EndZ=0
    g39: LineSegment StartX=859.697 StartY=85 StartZ=0 EndX=1685.36 EndY=491.669 EndZ=0
    g40: LineSegment StartX=-155 StartY=-25 StartZ=0 EndX=-155 EndY=-145 EndZ=0
    g41: LineSegment StartX=-155 StartY=-145 StartZ=0 EndX=-170 EndY=-185 EndZ=0
    g42: LineSegment StartX=-170 StartY=-185 StartZ=0 EndX=-269.574 EndY=-464.164 EndZ=0
    g43: LineSegment StartX=-269.574 StartY=-464.164 StartZ=0 EndX=-470 EndY=-970 EndZ=0
    g44: LineSegment StartX=-470 StartY=-970 StartZ=0 EndX=-650 EndY=-970 EndZ=0
    g45: LineSegment StartX=-650 StartY=-970 StartZ=0 EndX=-235 EndY=-165 EndZ=0
    g46: LineSegment StartX=-235 StartY=-165 StartZ=0 EndX=-235 EndY=-25 EndZ=0
    g47: LineSegment StartX=-235 StartY=-25 StartZ=0 EndX=-155 EndY=-25 EndZ=0
    g48: LineSegment StartX=155 StartY=-25 StartZ=0 EndX=155 EndY=-145 EndZ=0
    g49: LineSegment StartX=155 StartY=-145 StartZ=0 EndX=170 EndY=-185 EndZ=0
    g50: LineSegment StartX=170 StartY=-185 StartZ=0 EndX=269.574 EndY=-464.164 EndZ=0
    g51: LineSegment StartX=269.574 StartY=-464.164 StartZ=0 EndX=470 EndY=-970 EndZ=0
    g52: LineSegment StartX=470 StartY=-970 StartZ=0 EndX=650 EndY=-970 EndZ=0
    g53: LineSegment StartX=650 StartY=-970 StartZ=0 EndX=235 EndY=-165 EndZ=0
    g54: LineSegment StartX=235 StartY=-165 StartZ=0 EndX=235 EndY=-25 EndZ=0
    g55: LineSegment StartX=235 StartY=-25 StartZ=0 EndX=155 EndY=-25 EndZ=0
    g56: LineSegment StartX=-235 StartY=85 StartZ=0 EndX=-155 EndY=85 EndZ=0
    g57: LineSegment StartX=-155 StartY=85 StartZ=0 EndX=-155 EndY=205 EndZ=0
    g58: LineSegment StartX=-155 StartY=205 StartZ=0 EndX=-684.039 EndY=1030 EndZ=0
    g59: LineSegment StartX=-684.039 StartY=1030 StartZ=0 EndX=-834.039 EndY=1030 EndZ=0
    g60: LineSegment StartX=-834.039 StartY=1030 StartZ=0 EndX=-235 EndY=225 EndZ=0
    g61: LineSegment StartX=-235 StartY=225 StartZ=0 EndX=-235 EndY=85 EndZ=0
    g62: LineSegment StartX=235 StartY=85 StartZ=0 EndX=155 EndY=85 EndZ=0
    g63: LineSegment StartX=155 StartY=85 StartZ=0 EndX=155 EndY=205 EndZ=0
    g64: LineSegment StartX=155 StartY=205 StartZ=0 EndX=684.039 EndY=1030 EndZ=0
    g65: LineSegment StartX=684.039 StartY=1030 StartZ=0 EndX=834.039 EndY=1030 EndZ=0
    g66: LineSegment StartX=834.039 StartY=1030 StartZ=0 EndX=235 EndY=225 EndZ=0
    g67: LineSegment StartX=235 StartY=225 StartZ=0 EndX=235 EndY=85 EndZ=0
    g68: LineSegment StartX=105 StartY=-25 StartZ=0 EndX=25 EndY=-25 EndZ=0
    g69: LineSegment StartX=25 StartY=-25 StartZ=0 EndX=25 EndY=-145 EndZ=0
    g70: LineSegment StartX=25 StartY=-145 StartZ=0 EndX=53.655 EndY=-503.461 EndZ=0
    g71: LineSegment StartX=53.655 StartY=-503.461 StartZ=0 EndX=100 EndY=-970 EndZ=0
    g72: LineSegment StartX=100 StartY=-970 StartZ=0 EndX=250 EndY=-970 EndZ=0
    g73: LineSegment StartX=250 StartY=-970 StartZ=0 EndX=105 EndY=-205 EndZ=0
    g74: LineSegment StartX=105 StartY=-205 StartZ=0 EndX=105 EndY=-25 EndZ=0
    g75: LineSegment StartX=-105 StartY=-25 StartZ=0 EndX=-25 EndY=-25 EndZ=0
    g76: LineSegment StartX=-25 StartY=-25 StartZ=0 EndX=-25 EndY=-145 EndZ=0
    g77: LineSegment StartX=-25 StartY=-145 StartZ=0 EndX=-53.655 EndY=-503.461 EndZ=0
    g78: LineSegment StartX=-53.655 StartY=-503.461 StartZ=0 EndX=-100 EndY=-970 EndZ=0
    g79: LineSegment StartX=-100 StartY=-970 StartZ=0 EndX=-250 EndY=-970 EndZ=0
    g80: LineSegment StartX=-250 StartY=-970 StartZ=0 EndX=-105 EndY=-205 EndZ=0
    g81: LineSegment StartX=-105 StartY=-205 StartZ=0 EndX=-105 EndY=-25 EndZ=0
  constraints (122):
    c: Coincident(g0,g1)
    c: Coincident(g1,g2)
    c: Coincident(g2,g3)
    c: Horizontal(g3)
    c: Coincident(g3,g4)
    c: Coincident(g4,g5)
    c: Vertical(g5)
    c: Coincident(g5,g6)
    c: Horizontal(g6)
    c: Coincident(g6,g7)
    c: Coincident(g7,g0)
    c: Coincident(g8,g9)
    c: Coincident(g9,g10)
    c: Coincident(g10,g11)
    c: Horizontal(g11)
    c: Coincident(g11,g12)
    c: Coincident(g12,g13)
    c: Vertical(g13)
    c: Coincident(g13,g14)
    c: Horizontal(g14)
    c: Coincident(g14,g15)
    c: Coincident(g15,g8)
    c: Coincident(g16,g17)
    c: Coincident(g17,g18)
    c: Coincident(g18,g19)
    c: Horizontal(g19)
    c: Coincident(g19,g20)
    c: Coincident(g20,g21)
    c: Vertical(g21)
    c: Coincident(g21,g22)
    c: Horizontal(g22)
    c: Coincident(g22,g23)
    c: Coincident(g23,g16)
    c: Coincident(g24,g25)
    c: Vertical(g25)
    c: Coincident(g25,g26)
    c: Horizontal(g26)
    c: Coincident(g26,g27)
    c: Vertical(g27)
    c: Coincident(g27,g28)
    c: Coincident(g28,g29)
    c: Coincident(g29,g30)
    c: Horizontal(g30)
    c: Coincident(g30,g31)
    c: Coincident(g31,g24)
    c: Coincident(g32,g33)
    c: Coincident(g33,g34)
    c: Coincident(g34,g35)
    c: Horizontal(g35)
    c: Coincident(g35,g36)
    c: Coincident(g36,g37)
    c: Vertical(g37)
    c: Coincident(g37,g38)
    c: Horizontal(g38)
    c: Coincident(g38,g39)
    c: Coincident(g39,g32)
    c: Vertical(g40)
    c: Coincident(g40,g41)
    c: Coincident(g41,g42)
    c: Coincident(g42,g43)
    c: Coincident(g43,g44)
    c: Horizontal(g44)
    c: Coincident(g44,g45)
    c: Coincident(g45,g46)
    c: Vertical(g46)
    c: Coincident(g46,g47)
    c: Horizontal(g47)
    c: Coincident(g47,g40)
    c: Vertical(g48)
    c: Coincident(g48,g49)
    c: Coincident(g49,g50)
    c: Coincident(g50,g51)
    c: Coincident(g51,g52)
    c: Horizontal(g52)
    c: Coincident(g52,g53)
    c: Coincident(g53,g54)
    c: Vertical(g54)
    c: Coincident(g54,g55)
    c: Horizontal(g55)
    c: Coincident(g55,g48)
    c: Horizontal(g56)
    c: Coincident(g56,g57)
    c: Vertical(g57)
    c: Coincident(g57,g58)
    c: Coincident(g58,g59)
    c: Horizontal(g59)
    c: Coincident(g59,g60)
    c: Coincident(g60,g61)
    c: Vertical(g61)
    c: Coincident(g61,g56)
    c: Horizontal(g62)
    c: Coincident(g62,g63)
    c: Vertical(g63)
    c: Coincident(g63,g64)
    c: Coincident(g64,g65)
    c: Horizontal(g65)
    c: Coincident(g65,g66)
    c: Coincident(g66,g67)
    c: Vertical(g67)
    c: Coincident(g67,g62)
    c: Horizontal(g68)
    c: Coincident(g68,g69)
    c: Vertical(g69)
    c: Coincident(g69,g70)
    c: Coincident(g70,g71)
    c: Coincident(g71,g72)
    c: Horizontal(g72)
    c: Coincident(g72,g73)
    c: Coincident(g73,g74)
    c: Vertical(g74)
    c: Coincident(g74,g68)
    c: Horizontal(g75)
    c: Coincident(g75,g76)
    c: Vertical(g76)
    c: Coincident(g76,g77)
    c: Coincident(g77,g78)
    c: Coincident(g78,g79)
    c: Horizontal(g79)
    c: Coincident(g79,g80)
    c: Coincident(g80,g81)
    c: Vertical(g81)
    c: Coincident(g81,g75)
FEATURE [Sketcher::SketchObject] Sketch026
  sketch-geometry (58):
    g0: LineSegment StartX=450 StartY=-970 StartZ=0 EndX=170 EndY=-185 EndZ=0
    g1: LineSegment StartX=170 StartY=-185 StartZ=0 EndX=170 EndY=-25 EndZ=0
    g2: LineSegment StartX=170 StartY=-25 StartZ=0 EndX=90 EndY=-25 EndZ=0
    g3: LineSegment StartX=90 StartY=-25 StartZ=0 EndX=90 EndY=-145 EndZ=0
    g4: LineSegment StartX=90 StartY=-145 StartZ=0 EndX=133.61 EndY=-355.94 EndZ=0
    g5: LineSegment StartX=133.61 StartY=-355.94 StartZ=0 EndX=300 EndY=-970 EndZ=0
    g6: LineSegment StartX=300 StartY=-970 StartZ=0 EndX=450 EndY=-970 EndZ=0
    g7: LineSegment StartX=-40 StartY=-205 StartZ=0 EndX=-40 EndY=-25 EndZ=0
    g8: LineSegment StartX=-40 StartY=-25 StartZ=0 EndX=40 EndY=-25 EndZ=0
    g9: LineSegment StartX=40 StartY=-25 StartZ=0 EndX=40 EndY=-205 EndZ=0
    g10: LineSegment StartX=40 StartY=-205 StartZ=0 EndX=75 EndY=-970 EndZ=0
    g11: LineSegment StartX=75 StartY=-970 StartZ=0 EndX=-75 EndY=-970 EndZ=0
    g12: LineSegment StartX=-75 StartY=-970 StartZ=0 EndX=-40 EndY=-205 EndZ=0
    g13: LineSegment StartX=-450 StartY=-970 StartZ=0 EndX=-170 EndY=-185 EndZ=0
    g14: LineSegment StartX=-170 StartY=-185 StartZ=0 EndX=-170 EndY=-25 EndZ=0
    g15: LineSegment StartX=-170 StartY=-25 StartZ=0 EndX=-90 EndY=-25 EndZ=0
    g16: LineSegment StartX=-90 StartY=-25 StartZ=0 EndX=-90 EndY=-145 EndZ=0
    g17: LineSegment StartX=-90 StartY=-145 StartZ=0 EndX=-133.61 EndY=-355.94 EndZ=0
    g18: LineSegment StartX=-133.61 StartY=-355.94 StartZ=0 EndX=-300 EndY=-970 EndZ=0
    g19: LineSegment StartX=-300 StartY=-970 StartZ=0 EndX=-450 EndY=-970 EndZ=0
    g20: LineSegment StartX=-850 StartY=-970 StartZ=0 EndX=-300 EndY=-145 EndZ=0
    g21: LineSegment StartX=-300 StartY=-145 StartZ=0 EndX=-300 EndY=-25 EndZ=0
    g22: LineSegment StartX=-300 StartY=-25 StartZ=0 EndX=-220 EndY=-25 EndZ=0
    g23: LineSegment StartX=-220 StartY=-25 StartZ=0 EndX=-220 EndY=-145 EndZ=0
    g24: LineSegment StartX=-220 StartY=-145 StartZ=0 EndX=-368.439 EndY=-423.84 EndZ=0
    g25: LineSegment StartX=-368.439 StartY=-423.84 StartZ=0 EndX=-670 EndY=-970 EndZ=0
    g26: LineSegment StartX=-670 StartY=-970 StartZ=0 EndX=-850 EndY=-970 EndZ=0
    g27: LineSegment StartX=-674.039 StartY=1030 StartZ=0 EndX=-170 EndY=245 EndZ=0
    g28: LineSegment StartX=-170 StartY=245 StartZ=0 EndX=-170 EndY=85 EndZ=0
    g29: LineSegment StartX=-170 StartY=85 StartZ=0 EndX=-90 EndY=85 EndZ=0
    g30: LineSegment StartX=-90 StartY=85 StartZ=0 EndX=-90 EndY=245 EndZ=0
    g31: LineSegment StartX=-90 StartY=245 StartZ=0 EndX=-524.039 EndY=1030 EndZ=0
    g32: LineSegment StartX=-524.039 StartY=1030 StartZ=0 EndX=-674.039 EndY=1030 EndZ=0
    g33: LineSegment StartX=1000 StartY=1030 StartZ=0 EndX=300 EndY=205 EndZ=0
    g34: LineSegment StartX=300 StartY=205 StartZ=0 EndX=300 EndY=85 EndZ=0
    g35: LineSegment StartX=300 StartY=85 StartZ=0 EndX=220 EndY=85 EndZ=0
    g36: LineSegment StartX=220 StartY=85 StartZ=0 EndX=220 EndY=205 EndZ=0
    g37: LineSegment StartX=220 StartY=205 StartZ=0 EndX=850 EndY=1030 EndZ=0
    g38: LineSegment StartX=850 StartY=1030 StartZ=0 EndX=1000 EndY=1030 EndZ=0
    g39: LineSegment StartX=850 StartY=-970 StartZ=0 EndX=300 EndY=-145 EndZ=0
    g40: LineSegment StartX=300 StartY=-145 StartZ=0 EndX=300 EndY=-25 EndZ=0
    g41: LineSegment StartX=300 StartY=-25 StartZ=0 EndX=220 EndY=-25 EndZ=0
    g42: LineSegment StartX=220 StartY=-25 StartZ=0 EndX=220 EndY=-145 EndZ=0
    g43: LineSegment StartX=220 StartY=-145 StartZ=0 EndX=368.439 EndY=-423.84 EndZ=0
    g44: LineSegment StartX=368.439 StartY=-423.84 StartZ=0 EndX=670 EndY=-970 EndZ=0
    g45: LineSegment StartX=670 StartY=-970 StartZ=0 EndX=850 EndY=-970 EndZ=0
    g46: LineSegment StartX=-1000 StartY=1030 StartZ=0 EndX=-300 EndY=205 EndZ=0
    g47: LineSegment StartX=-300 StartY=205 StartZ=0 EndX=-300 EndY=85 EndZ=0
    g48: LineSegment StartX=-300 StartY=85 StartZ=0 EndX=-220 EndY=85 EndZ=0
    g49: LineSegment StartX=-220 StartY=85 StartZ=0 EndX=-220 EndY=205 EndZ=0
    g50: LineSegment StartX=-220 StartY=205 StartZ=0 EndX=-850 EndY=1030 EndZ=0
    g51: LineSegment StartX=-850 StartY=1030 StartZ=0 EndX=-1000 EndY=1030 EndZ=0
    g52: LineSegment StartX=674.039 StartY=1030 StartZ=0 EndX=170 EndY=245 EndZ=0
    g53: LineSegment StartX=170 StartY=245 StartZ=0 EndX=170 EndY=85 EndZ=0
    g54: LineSegment StartX=170 StartY=85 StartZ=0 EndX=90 EndY=85 EndZ=0
    g55: LineSegment StartX=90 StartY=85 StartZ=0 EndX=90 EndY=245 EndZ=0
    g56: LineSegment StartX=90 StartY=245 StartZ=0 EndX=524.039 EndY=1030 EndZ=0
    g57: LineSegment StartX=524.039 StartY=1030 StartZ=0 EndX=674.039 EndY=1030 EndZ=0
  constraints (94):
    c: Coincident(g0,g1)
    c: Vertical(g1)
    c: Coincident(g1,g2)
    c: Horizontal(g2)
    c: Coincident(g2,g3)
    c: Vertical(g3)
    c: Coincident(g3,g4)
    c: Coincident(g4,g5)
    c: Coincident(g5,g6)
    c: Horizontal(g6)
    c: Coincident(g6,g0)
    c: Vertical(g7)
    c: Coincident(g7,g8)
    c: Horizontal(g8)
    c: Coincident(g8,g9)
    c: Vertical(g9)
    c: Coincident(g9,g10)
    c: Coincident(g10,g11)
    c: Horizontal(g11)
    c: Coincident(g11,g12)
    c: Coincident(g12,g7)
    c: Coincident(g13,g14)
    c: Vertical(g14)
    c: Coincident(g14,g15)
    c: Horizontal(g15)
    c: Coincident(g15,g16)
    c: Vertical(g16)
    c: Coincident(g16,g17)
    c: Coincident(g17,g18)
    c: Coincident(g18,g19)
    c: Horizontal(g19)
    c: Coincident(g19,g13)
    c: Coincident(g20,g21)
    c: Vertical(g21)
    c: Coincident(g21,g22)
    c: Horizontal(g22)
    c: Coincident(g22,g23)
    c: Vertical(g23)
    c: Coincident(g23,g24)
    c: Coincident(g24,g25)
    c: Coincident(g25,g26)
    c: Horizontal(g26)
    c: Coincident(g26,g20)
    c: Coincident(g27,g28)
    c: Vertical(g28)
    c: Coincident(g28,g29)
    c: Horizontal(g29)
    c: Coincident(g29,g30)
    c: Vertical(g30)
    c: Coincident(g30,g31)
    c: Coincident(g31,g32)
    c: Horizontal(g32)
    c: Coincident(g32,g27)
    c: Coincident(g33,g34)
    c: Vertical(g34)
    c: Coincident(g34,g35)
    c: Horizontal(g35)
    c: Coincident(g35,g36)
    c: Vertical(g36)
    c: Coincident(g36,g37)
    c: Coincident(g37,g38)
    c: Horizontal(g38)
    c: Coincident(g38,g33)
    c: Coincident(g39,g40)
    c: Vertical(g40)
    c: Coincident(g40,g41)
    c: Horizontal(g41)
    c: Coincident(g41,g42)
    c: Vertical(g42)
    c: Coincident(g42,g43)
    c: Coincident(g43,g44)
    c: Coincident(g44,g45)
    c: Horizontal(g45)
    c: Coincident(g45,g39)
    c: Coincident(g46,g47)
    c: Vertical(g47)
    c: Coincident(g47,g48)
    c: Horizontal(g48)
    c: Coincident(g48,g49)
    c: Vertical(g49)
    c: Coincident(g49,g50)
    c: Coincident(g50,g51)
    c: Horizontal(g51)
    c: Coincident(g51,g46)
    c: Coincident(g52,g53)
    c: Vertical(g53)
    c: Coincident(g53,g54)
    c: Horizontal(g54)
    c: Coincident(g54,g55)
    c: Vertical(g55)
    c: Coincident(g55,g56)
    c: Coincident(g56,g57)
    c: Horizontal(g57)
    c: Coincident(g57,g52)
FEATURE [Sketcher::SketchObject] Sketch027
  sketch-geometry (4):
    g0: LineSegment StartX=1755.58 StartY=-1060.05 StartZ=0 EndX=-1734.89 EndY=-1060.05 EndZ=0
    g1: LineSegment StartX=-1734.89 StartY=-1060.05 StartZ=0 EndX=-1734.89 EndY=1108.73 EndZ=0
    g2: LineSegment StartX=-1734.89 StartY=1108.73 StartZ=0 EndX=1755.58 EndY=1108.73 EndZ=0
    g3: LineSegment StartX=1755.58 StartY=1108.73 StartZ=0 EndX=1755.58 EndY=-1060.05 EndZ=0
  constraints (8):
    c: Coincident(g0,g1)
    c: Coincident(g1,g2)
    c: Coincident(g2,g3)
    c: Coincident(g3,g0)
    c: Horizontal(g0)
    c: Horizontal(g2)
    c: Vertical(g1)
    c: Vertical(g3)
FEATURE [Sketcher::SketchObject] Sketch028
  sketch-geometry (4):
    g0: LineSegment StartX=1755.58 StartY=-1060.05 StartZ=0 EndX=-1734.89 EndY=-1060.05 EndZ=0
    g1: LineSegment StartX=-1734.89 StartY=-1060.05 StartZ=0 EndX=-1734.89 EndY=1108.73 EndZ=0
    g2: LineSegment StartX=-1734.89 StartY=1108.73 StartZ=0 EndX=1755.58 EndY=1108.73 EndZ=0
    g3: LineSegment StartX=1755.58 StartY=1108.73 StartZ=0 EndX=1755.58 EndY=-1060.05 EndZ=0
  constraints (8):
    c: Coincident(g0,g1)
    c: Coincident(g1,g2)
    c: Coincident(g2,g3)
    c: Coincident(g3,g0)
    c: Horizontal(g0)
    c: Horizontal(g2)
    c: Vertical(g1)
    c: Vertical(g3)
FEATURE [Sketcher::SketchObject] Sketch029
  sketch-geometry (4):
    g0: LineSegment StartX=1755.58 StartY=-1060.05 StartZ=0 EndX=-1734.89 EndY=-1060.05 EndZ=0
    g1: LineSegment StartX=-1734.89 StartY=-1060.05 StartZ=0 EndX=-1734.89 EndY=1108.73 EndZ=0
    g2: LineSegment StartX=-1734.89 StartY=1108.73 StartZ=0 EndX=1755.58 EndY=1108.73 EndZ=0
    g3: LineSegment StartX=1755.58 StartY=1108.73 StartZ=0 EndX=1755.58 EndY=-1060.05 EndZ=0
  constraints (8):
    c: Coincident(g0,g1)
    c: Coincident(g1,g2)
    c: Coincident(g2,g3)
    c: Coincident(g3,g0)
    c: Horizontal(g0)
    c: Horizontal(g2)
    c: Vertical(g1)
    c: Vertical(g3)
